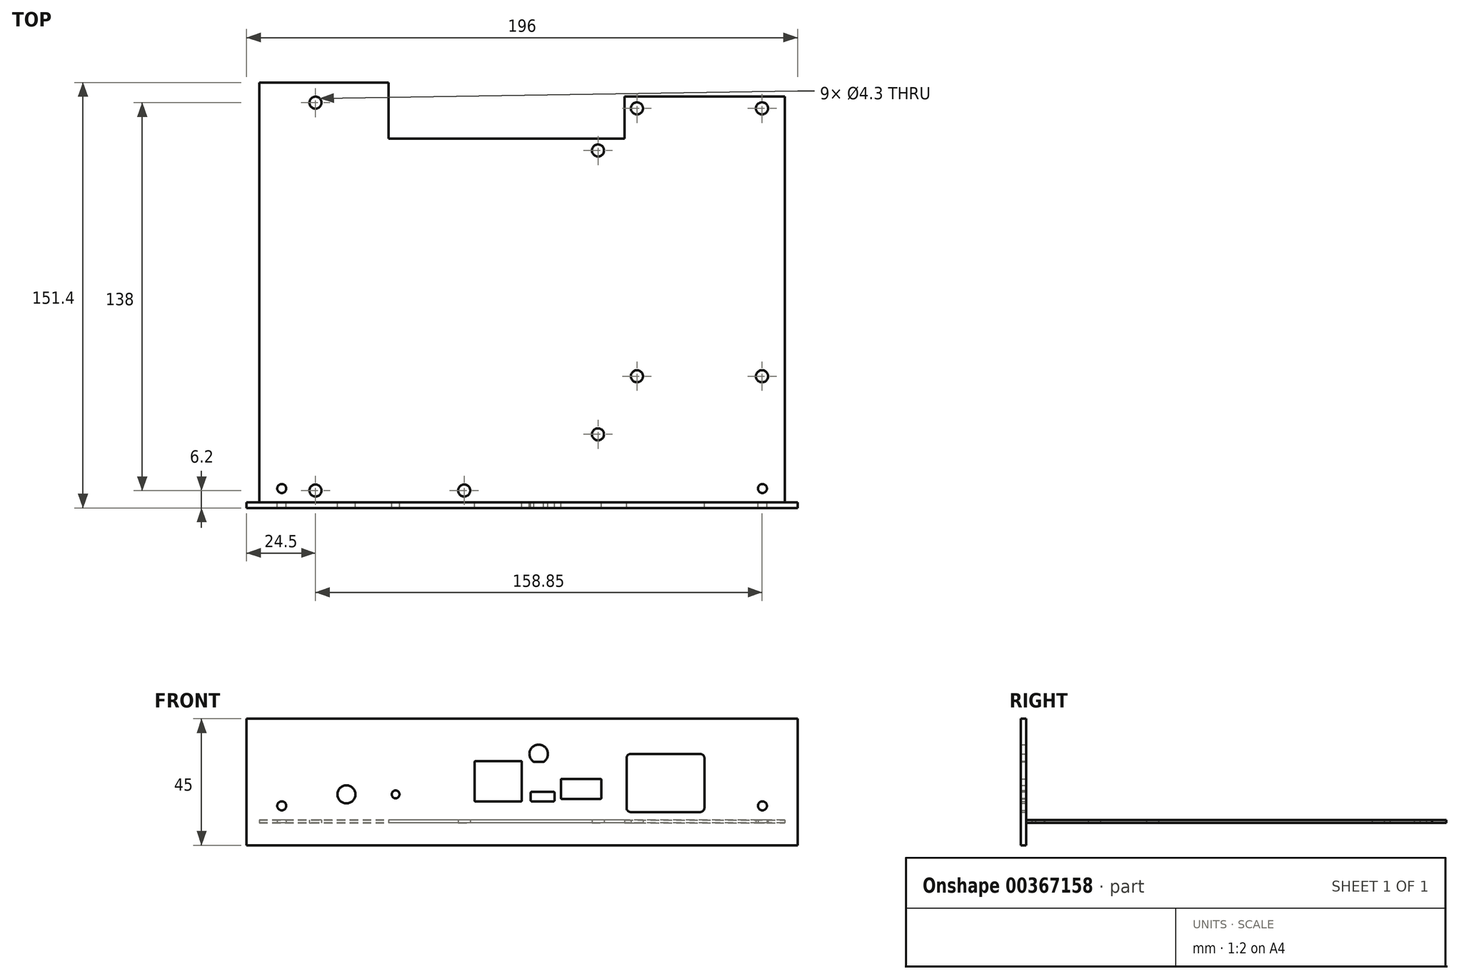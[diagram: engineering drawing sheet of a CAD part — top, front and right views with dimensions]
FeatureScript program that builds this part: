
annotation { "Feature Type Name" : "Feature", "Feature Type Description" : "" }
export const myFeature = defineFeature(function(context is Context, id is Id, definition is map)
    precondition{}
    {
        {
            var Q0;
            Q0=qCreatedBy(makeId("Top.planeOp"),FACE);
            var sketch = newSketch(context, id + "F0", { "sketchPlane" : qUnion([Q0])});
            skLineSegment(sketch, "E0", {"start": v(34, 47.2) * mm, "end": v(-50, 47.2) * mm});
            skLineSegment(sketch, "E1", {"start": v(-50, 47.2) * mm, "end": v(-50, 67.2) * mm});
            skLineSegment(sketch, "E2", {"start": v(34, 47.2) * mm, "end": v(34, 62.2) * mm});
            skLineSegment(sketch, "E3", {"start": v(-96, 67.2) * mm, "end": v(-50, 67.2) * mm});
            skLineSegment(sketch, "E4", {"start": v(34, 62.2) * mm, "end": v(91, 62.2) * mm});
            skLineSegment(sketch, "E5", {"start": v(91, 62.2) * mm, "end": v(91, -82.2) * mm});
            skLineSegment(sketch, "E6", {"start": v(91, -82.2) * mm, "end": v(-96, -82.2) * mm});
            skLineSegment(sketch, "E7", {"start": v(-96, 67.2) * mm, "end": v(-96, -82.2) * mm});
            skCircle(sketch, "E8", {"center": v(-88, -77.3) * mm, "radius": 1.6 * mm});
            skCircle(sketch, "E9", {"center": v(83, -77.3) * mm, "radius": 1.6 * mm});
            skSolve(sketch);
        }
        {
            var Q0;
            Q0=qCreatedBy(makeId("Top.planeOp"),FACE);
            var sketch = newSketch(context, id + "F1", { "sketchPlane" : qUnion([Q0])});
            skLineSegment(sketch, "E10.bottom", {"start": v(-82.8, 64) * mm, "end": v(-82.8, -82) * mm, "construction": true});
            skLineSegment(sketch, "E10.top", {"start": v(28, 64) * mm, "end": v(28, -82) * mm, "construction": true});
            skLineSegment(sketch, "E10.left", {"start": v(-82.8, 64) * mm, "end": v(28, 64) * mm, "construction": true});
            skLineSegment(sketch, "E10.right", {"start": v(-82.8, -82) * mm, "end": v(28, -82) * mm, "construction": true});
            skPoint(sketch, "E10.middle", {"position": v(-27.4, -9) * mm});
            skCircle(sketch, "E11", {"center": v(-76, -78) * mm, "radius": 1.5 * mm});
            skCircle(sketch, "E12", {"center": v(-23.1, -78) * mm, "radius": 1.5 * mm});
            skCircle(sketch, "E13", {"center": v(24.5, -58) * mm, "radius": 1.5 * mm});
            skCircle(sketch, "E14", {"center": v(24.5, 43) * mm, "radius": 1.5 * mm});
            skCircle(sketch, "E15", {"center": v(-76, 60) * mm, "radius": 1.5 * mm});
            skSolve(sketch);
        }
        {
            var Q0;
            Q0=qCreatedBy(makeId("Top.planeOp"),FACE);
            var sketch = newSketch(context, id + "F2", { "sketchPlane" : qUnion([Q0])});
            skLineSegment(sketch, "E16.bottom", {"start": v(86, -40.5) * mm, "end": v(86, 61.1) * mm, "construction": true});
            skLineSegment(sketch, "E16.top", {"start": v(35.2, -40.5) * mm, "end": v(35.2, 61.1) * mm, "construction": true});
            skLineSegment(sketch, "E16.left", {"start": v(86, -40.5) * mm, "end": v(35.2, -40.5) * mm, "construction": true});
            skLineSegment(sketch, "E16.right", {"start": v(86, 61.1) * mm, "end": v(35.2, 61.1) * mm, "construction": true});
            skPoint(sketch, "E16.middle", {"position": v(60.6, 10.3) * mm});
            skCircle(sketch, "E17", {"center": v(82.85, 57.98) * mm, "radius": 1.65 * mm});
            skCircle(sketch, "E18", {"center": v(82.85, -37.32) * mm, "radius": 1.65 * mm});
            skCircle(sketch, "E19", {"center": v(38.35, 57.98) * mm, "radius": 1.65 * mm});
            skCircle(sketch, "E20", {"center": v(38.35, -37.32) * mm, "radius": 1.65 * mm});
            skSolve(sketch);
        }
        {
            var Q0;
            Q0=qSketchRegion(id+"F0",true);
            extrude(context, id + "F3", {"entities" : qUnion([Q0]), "depth" : 1 * mm});
        }
        {
            var Q0;
            Q0=sQuery(id+"F1.wireOp",VERTEX,"E15.center");
            var Q1;
            Q1=sQuery(id+"F1.wireOp",VERTEX,"E11.center");
            var Q2;
            Q2=sQuery(id+"F1.wireOp",VERTEX,"E12.center");
            var Q3;
            Q3=sQuery(id+"F1.wireOp",VERTEX,"E13.center");
            var Q4;
            Q4=sQuery(id+"F1.wireOp",VERTEX,"E14.center");
            var Q5;
            Q5=sQuery(id+"F2.wireOp",VERTEX,"E19.center");
            var Q6;
            Q6=sQuery(id+"F2.wireOp",VERTEX,"E17.center");
            var Q7;
            Q7=sQuery(id+"F2.wireOp",VERTEX,"E18.center");
            var Q8;
            Q8=sQuery(id+"F2.wireOp",VERTEX,"E20.center");
            var Q9;
            Q9=makeQuery(id+"F3.opExtrude","SWEPT_BODY",BODY,{"disambiguationData":[OSD([sQuery(id+"F0.wireOp",EDGE,"952b0ec7-d35d-4aa0-9ed3-2b37ddbb3af9.0"),sQuery(id+"F0.wireOp",EDGE,"952b0ec7-d35d-4aa0-9ed3-2b37ddbb3af9.1"),sQuery(id+"F0.wireOp",EDGE,"952b0ec7-d35d-4aa0-9ed3-2b37ddbb3af9.2"),sQuery(id+"F0.wireOp",EDGE,"952b0ec7-d35d-4aa0-9ed3-2b37ddbb3af9.3"),sQuery(id+"F0.wireOp",EDGE,"E0"),sQuery(id+"F0.wireOp",EDGE,"E1"),sQuery(id+"F0.wireOp",EDGE,"E2"),sQuery(id+"F0.wireOp",EDGE,"SLuukLqY-ycax-Xmuq-RENi-PwCJtmiq9tnc"),sQuery(id+"F0.wireOp",EDGE,"hQ4yqffv-p3Bx-uhC1-s7De-o8YXlfHT2a4Z"),sQuery(id+"F0.wireOp",EDGE,"061bc317-8ba2-4e4e-ab30-87023d86f5ae.trimOffspring"),sQuery(id+"F0.wireOp",EDGE,"72c2dd2a-2393-4d0f-b5e8-c2df332b1109.0"),sQuery(id+"F0.wireOp",EDGE,"d0d5820a-22a4-4be2-a90f-887b21bb4185.0"),sQuery(id+"F0.wireOp",EDGE,"52745bf9-f830-46ef-a72f-5fba75537b27.0"),sQuery(id+"F0.wireOp",EDGE,"2e9c58e6-5ac8-4968-8ab0-7c57b15c46ae.0"),sQuery(id+"F0.wireOp",EDGE,"f805605a-9e98-4eea-8f7f-1287431cd805.0"),sQuery(id+"F0.wireOp",EDGE,"ad351e9f-189b-4aa0-8342-32a5907348db.0"),sQuery(id+"F0.wireOp",EDGE,"ad55f3a1-77f3-4fa6-82f7-07b5f075875b.0"),sQuery(id+"F0.wireOp",EDGE,"6803d59f-041c-48d9-92b3-cae51df63e9c.0")])]});
            hole(context, id + "F4", {"style" : HoleStyle.SIMPLE, "endStyle" : HoleEndStyle.THROUGH, "oppositeDirection" : true, "standardTappedOrClearance" : lookupTablePath({ "standard" : "ISO", "size" : "4.3", "type" : "Drilled" }), "standardBlindInLast" : lookupTablePath({ "standard" : "ISO", "size" : "4.3", "type" : "Drilled" }), "holeDiameter" : 4.3 * mm, "startFromSketch" : true, "locations" : qUnion([Q0, Q1, Q2, Q3, Q4, Q5, Q6, Q7, Q8]), "scope" : qUnion([Q9]), "tappedDepth" : 12 * mm, "tapClearance" : 3});
        }
        {
            var Q0;
            Q0=qCreatedBy(makeId("Front.planeOp"),FACE);
            cPlane(context, id + "F5", {"entities" : qUnion([Q0]), "cplaneType" : CPlaneType.OFFSET, "offset" : 82.2 * mm, "width" : 150 * mm, "height" : 150 * mm});
        }
        {
            var Q0;
            Q0=qCreatedBy(id+"F5.planeOp",FACE);
            var sketch = newSketch(context, id + "F6", { "sketchPlane" : qUnion([Q0])});
            skLineSegment(sketch, "E21.bottom", {"start": v(-100.5, 37) * mm, "end": v(95.5, 37) * mm});
            skLineSegment(sketch, "E21.top", {"start": v(-100.5, -8) * mm, "end": v(95.5, -8) * mm});
            skLineSegment(sketch, "E21.left", {"start": v(-100.5, 37) * mm, "end": v(-100.5, -8) * mm});
            skLineSegment(sketch, "E21.right", {"start": v(95.5, 37) * mm, "end": v(95.5, -8) * mm});
            skSolve(sketch);
        }
        {
            var Q0;
            Q0=qCreatedBy(id+"F5.planeOp",FACE);
            var sketch = newSketch(context, id + "F7", { "sketchPlane" : qUnion([Q0])});
            skLineSegment(sketch, "E22.bottom", {"start": v(36.15, 3.8) * mm, "end": v(60.85, 3.8) * mm});
            skLineSegment(sketch, "E22.top", {"start": v(36.15, 24.5) * mm, "end": v(60.85, 24.5) * mm});
            skLineSegment(sketch, "E22.left", {"start": v(34.65, 5.3) * mm, "end": v(34.65, 23) * mm});
            skLineSegment(sketch, "E22.right", {"start": v(62.35, 5.3) * mm, "end": v(62.35, 23) * mm});
            skPoint(sketch, "E23.visualSharp", {"position": v(34.65, 24.5) * mm});
            skArc(sketch, "E23.filletArc", {"start": v(36.15, 24.5) * mm, "mid": v(35.09, 24.06) * mm, "end": v(34.65, 23) * mm});
            skPoint(sketch, "E24.visualSharp", {"position": v(34.65, 3.8) * mm});
            skArc(sketch, "E24.filletArc", {"start": v(34.65, 5.3) * mm, "mid": v(35.09, 4.24) * mm, "end": v(36.15, 3.8) * mm});
            skPoint(sketch, "E25.visualSharp", {"position": v(62.35, 3.8) * mm});
            skArc(sketch, "E25.filletArc", {"start": v(60.85, 3.8) * mm, "mid": v(61.91, 4.24) * mm, "end": v(62.35, 5.3) * mm});
            skPoint(sketch, "E26.visualSharp", {"position": v(62.35, 24.5) * mm});
            skArc(sketch, "E26.filletArc", {"start": v(62.35, 23) * mm, "mid": v(61.91, 24.06) * mm, "end": v(60.85, 24.5) * mm});
            skLineSegment(sketch, "E27", {"start": v(-99.44, 14.5) * mm, "end": v(88.52, 14.5) * mm, "construction": true});
            skLineSegment(sketch, "E28", {"start": v(-82.8, 7.6) * mm, "end": v(28, 7.6) * mm, "construction": true});
            skLineSegment(sketch, "E29", {"start": v(86, 5) * mm, "end": v(35.8, 5) * mm, "construction": true});
            skCircle(sketch, "E30", {"center": v(-65, 10.1) * mm, "radius": 3.2 * mm});
            skLineSegment(sketch, "E31.bottom", {"start": v(-19.1, 7.6) * mm, "end": v(-2.9, 7.6) * mm});
            skLineSegment(sketch, "E31.top", {"start": v(-19.1, 21.95) * mm, "end": v(-2.9, 21.95) * mm});
            skLineSegment(sketch, "E31.left", {"start": v(-19.4, 7.9) * mm, "end": v(-19.4, 21.65) * mm});
            skLineSegment(sketch, "E31.right", {"start": v(-2.6, 7.9) * mm, "end": v(-2.6, 21.65) * mm});
            skLineSegment(sketch, "E32.bottom", {"start": v(0.9, 7.6) * mm, "end": v(8.7, 7.6) * mm});
            skLineSegment(sketch, "E32.top", {"start": v(0.9, 11) * mm, "end": v(8.7, 11) * mm});
            skLineSegment(sketch, "E32.left", {"start": v(0.6, 7.9) * mm, "end": v(0.6, 10.7) * mm});
            skLineSegment(sketch, "E32.right", {"start": v(9, 7.9) * mm, "end": v(9, 10.7) * mm});
            skLineSegment(sketch, "E33.bottom", {"start": v(11.6, 8.5) * mm, "end": v(25.4, 8.5) * mm});
            skLineSegment(sketch, "E33.top", {"start": v(11.6, 15.6) * mm, "end": v(25.4, 15.6) * mm});
            skLineSegment(sketch, "E33.left", {"start": v(11.3, 8.8) * mm, "end": v(11.3, 15.3) * mm});
            skLineSegment(sketch, "E33.right", {"start": v(25.7, 8.8) * mm, "end": v(25.7, 15.3) * mm});
            skCircle(sketch, "E34", {"center": v(-47.5, 10.1) * mm, "radius": 1.4 * mm});
            skPoint(sketch, "E35.visualSharp", {"position": v(-19.4, 21.95) * mm});
            skArc(sketch, "E35.filletArc", {"start": v(-19.1, 21.95) * mm, "mid": v(-19.31, 21.86) * mm, "end": v(-19.4, 21.65) * mm});
            skPoint(sketch, "E36.visualSharp", {"position": v(-2.6, 21.95) * mm});
            skArc(sketch, "E36.filletArc", {"start": v(-2.6, 21.65) * mm, "mid": v(-2.69, 21.86) * mm, "end": v(-2.9, 21.95) * mm});
            skPoint(sketch, "E37.visualSharp", {"position": v(-19.4, 7.6) * mm});
            skArc(sketch, "E37.filletArc", {"start": v(-19.4, 7.9) * mm, "mid": v(-19.31, 7.69) * mm, "end": v(-19.1, 7.6) * mm});
            skPoint(sketch, "E38.visualSharp", {"position": v(9, 11) * mm});
            skArc(sketch, "E38.filletArc", {"start": v(9, 10.7) * mm, "mid": v(8.91, 10.91) * mm, "end": v(8.7, 11) * mm});
            skPoint(sketch, "E39.visualSharp", {"position": v(9, 7.6) * mm});
            skArc(sketch, "E39.filletArc", {"start": v(8.7, 7.6) * mm, "mid": v(8.91, 7.69) * mm, "end": v(9, 7.9) * mm});
            skPoint(sketch, "E40.visualSharp", {"position": v(25.7, 15.6) * mm});
            skArc(sketch, "E40.filletArc", {"start": v(25.7, 15.3) * mm, "mid": v(25.61, 15.51) * mm, "end": v(25.4, 15.6) * mm});
            skPoint(sketch, "E41.visualSharp", {"position": v(11.3, 15.6) * mm});
            skArc(sketch, "E41.filletArc", {"start": v(11.6, 15.6) * mm, "mid": v(11.39, 15.51) * mm, "end": v(11.3, 15.3) * mm});
            skPoint(sketch, "E42.visualSharp", {"position": v(11.3, 8.5) * mm});
            skArc(sketch, "E42.filletArc", {"start": v(11.3, 8.8) * mm, "mid": v(11.39, 8.59) * mm, "end": v(11.6, 8.5) * mm});
            skPoint(sketch, "E43.visualSharp", {"position": v(25.7, 8.5) * mm});
            skArc(sketch, "E43.filletArc", {"start": v(25.4, 8.5) * mm, "mid": v(25.61, 8.59) * mm, "end": v(25.7, 8.8) * mm});
            skLineSegment(sketch, "E44.bottom", {"start": v(33, 26.15) * mm, "end": v(64, 26.15) * mm, "construction": true});
            skLineSegment(sketch, "E44.top", {"start": v(33, 2.15) * mm, "end": v(64, 2.15) * mm, "construction": true});
            skLineSegment(sketch, "E44.left", {"start": v(33, 26.15) * mm, "end": v(33, 2.15) * mm, "construction": true});
            skLineSegment(sketch, "E44.right", {"start": v(64, 26.15) * mm, "end": v(64, 2.15) * mm, "construction": true});
            skArc(sketch, "E45", {"start": v(5.15, 21.7) * mm, "mid": v(3.4, 27.8) * mm, "end": v(1.65, 21.7) * mm});
            skLineSegment(sketch, "E46", {"start": v(1.65, 21.7) * mm, "end": v(5.15, 21.7) * mm});
            skCircle(sketch, "E47", {"center": v(-88, 6) * mm, "radius": 1.6 * mm});
            skCircle(sketch, "E48", {"center": v(83, 6) * mm, "radius": 1.6 * mm});
            skPoint(sketch, "E49.visualSharp", {"position": v(-2.6, 7.6) * mm});
            skArc(sketch, "E49.filletArc", {"start": v(-2.9, 7.6) * mm, "mid": v(-2.69, 7.69) * mm, "end": v(-2.6, 7.9) * mm});
            skPoint(sketch, "E50.visualSharp", {"position": v(0.6, 11) * mm});
            skArc(sketch, "E50.filletArc", {"start": v(0.9, 11) * mm, "mid": v(0.69, 10.91) * mm, "end": v(0.6, 10.7) * mm});
            skPoint(sketch, "E51.visualSharp", {"position": v(0.6, 7.6) * mm});
            skArc(sketch, "E51.filletArc", {"start": v(0.6, 7.9) * mm, "mid": v(0.69, 7.69) * mm, "end": v(0.9, 7.6) * mm});
            skSolve(sketch);
        }
        {
            var Q0;
            Q0 = qSketchRegion(id + "F6", true);
            extrude(context, id + "F8", {"entities" : qUnion([Q0]), "depth" : 2 * mm});
        }
        {
            var Q0;
            Q0 = qSketchRegion(id + "F7", true);
            extrude(context, id + "F9", {"entities" : qUnion([Q0]), "operationType" : NewBodyOperationType.REMOVE, "endBound" : BoundingType.THROUGH_ALL, "depth" : 25 * mm});
        }
    });
